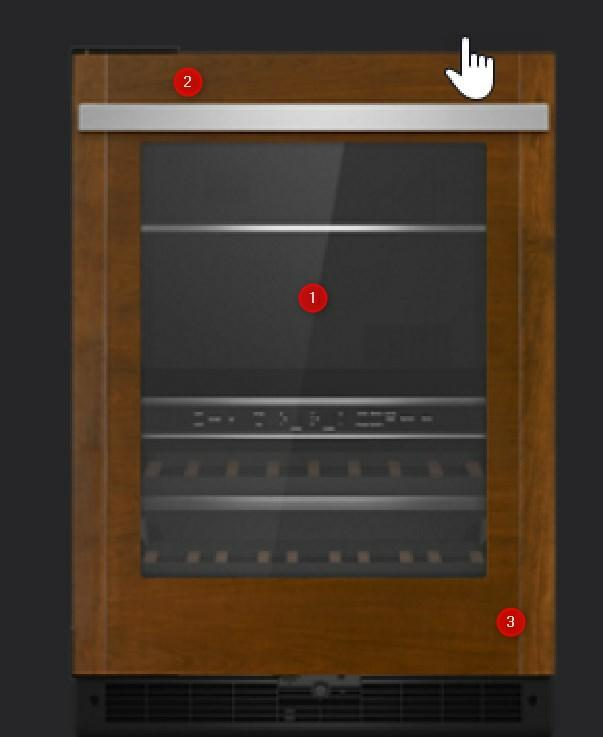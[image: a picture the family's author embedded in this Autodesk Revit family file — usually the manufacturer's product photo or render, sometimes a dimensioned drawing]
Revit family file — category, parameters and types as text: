
# Revit family: P210876JX-007_JUGFL242HX_JUGFR242HX
name_source: partatom
category: Specialty Equipment
units: mm (PartAtom-declared; Revit-internal decimal feet)

## family parameters
Always vertical = Yes
Cut with Voids When Loaded = No
Enable Cutting in Views = No
Maintain Annotation Orientation = No
Part Type = Normal
Room Calculation Point = No
Round Connector Dimension = Use Diameter
Shared = No
Work Plane-Based = No

## types (1)
- JUGFL242HX
    Amps = 0 A
    Back Panel Material = ARCAT - Metal - Aluminum
    Body Material = ARCAT - Metal - Steel - Black
    Bottom Panel Material = ARCAT - Metal - Steel - Black
    Clearance Material = ARCAT - Clearance
    Default Elevation = 0"
    Depth = 23 11/16"
    Description = Panel-Ready 24" Under Counter Glass Door Refrigerator, Left Swing
Réfrigérateur à porte en verre sous le comptoir, charnière à gauche, prêt pour le panneau, 24 po
    Dimension Guide = https://whirlpool.com
https://whirlpool.com
    Door Material = ARCAT - Metal - Steel - Black - Light
    Energy Guide = https://www.whirlpool.com
https://www.whirlpool.com
    Family Name = Undercounter Specialty
    Feature 1 = UV-Resistant Low-E Thermal Glass
Porte en verre thermique à faible émissivité résistant aux UV
    Feature 2 = Daring Obsidian Interior
Daring Obsidian Interior
    Feature 3 = Emotive Controls
Emotive Controls
    Glass Material = ARCAT - Glass - Gray
    Handle Material = ARCAT - Metal - Brass
    Height = 34 1/8"
    Hinge Material = ARCAT - Plastic - Black
    Leg Material = ARCAT - Plastic - Black
    Manufacturer = JennAir
    Model = JUGFL242HX
    Screw Material = ARCAT - Metal - Steel - Stainless
    Tray Material = ARCAT - Metal - Steel - Stainless
    Voltage = 0 V
    Width = 23 7/8"

## geometry (parser evidence)
native form markers: Sweep x2
no freeform markers — native parametric forms only
